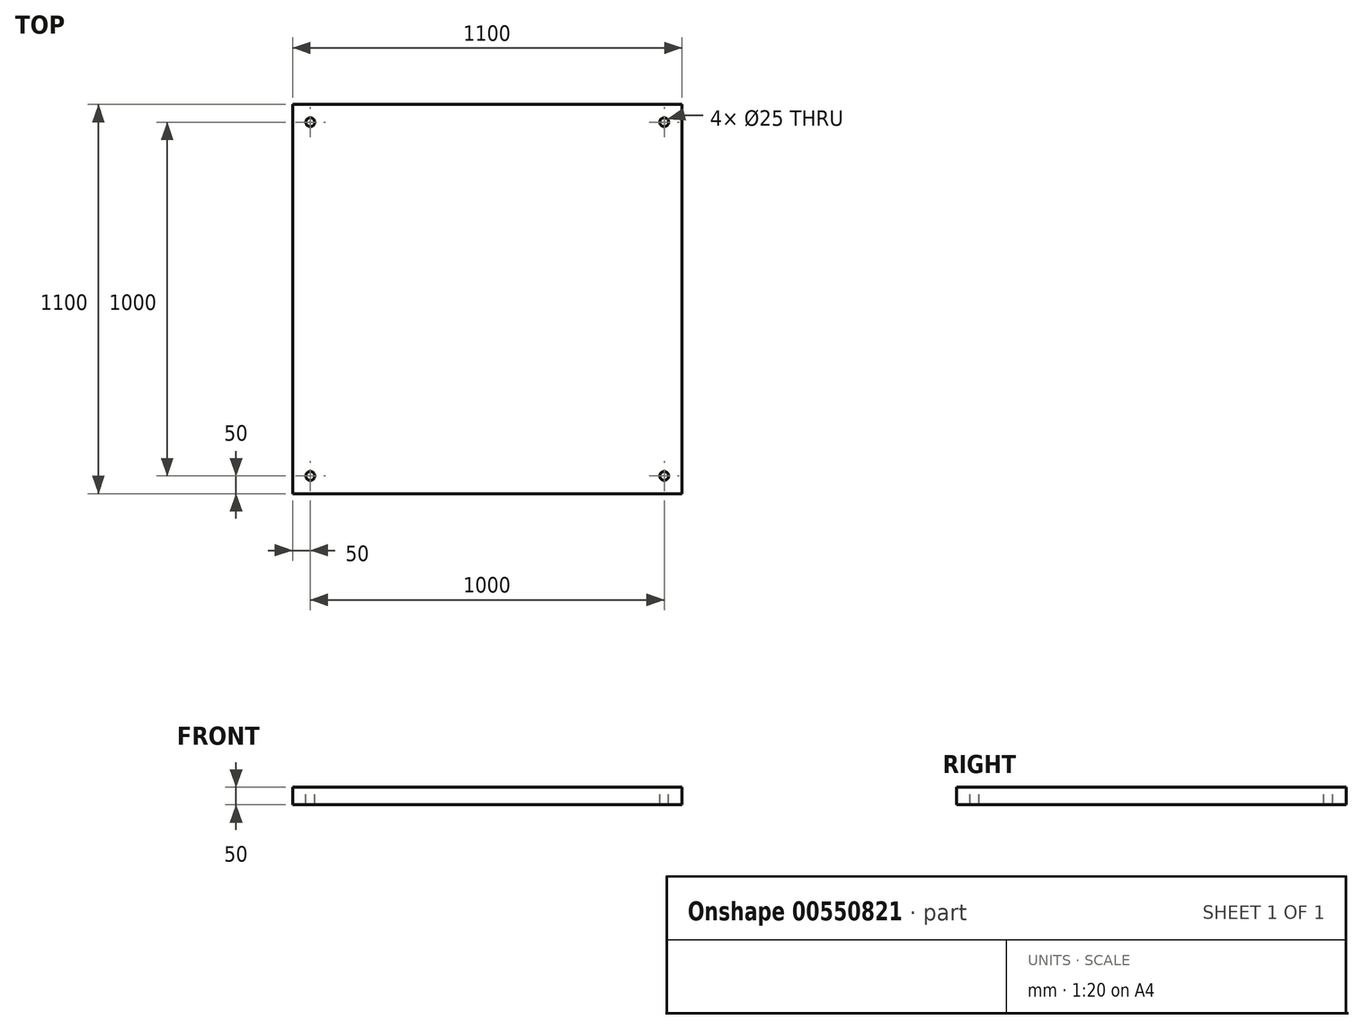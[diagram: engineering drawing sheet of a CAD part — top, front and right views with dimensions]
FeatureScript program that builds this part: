
annotation { "Feature Type Name" : "Feature", "Feature Type Description" : "" }
export const myFeature = defineFeature(function(context is Context, id is Id, definition is map)
    precondition{}
    {
        {
            var Q0;
            Q0=qCreatedBy(makeId("Top.planeOp"),FACE);
            var sketch = newSketch(context, id + "F0", { "sketchPlane" : qUnion([Q0])});
            skLineSegment(sketch, "E0.bottom", {"start": v(550, 550) * mm, "end": v(-550, 550) * mm});
            skLineSegment(sketch, "E0.top", {"start": v(550, -550) * mm, "end": v(-550, -550) * mm});
            skLineSegment(sketch, "E0.left", {"start": v(550, 550) * mm, "end": v(550, -550) * mm});
            skLineSegment(sketch, "E0.right", {"start": v(-550, 550) * mm, "end": v(-550, -550) * mm});
            skPoint(sketch, "E0.middle", {"position": v(0, 0) * mm});
            skSolve(sketch);
        }
        {
            var Q0;
            Q0=makeQuery(id+"F0.imprint","IMPRINT",FACE,{"disambiguationData":[TD([[makeQuery(id+"F0.imprint","IMPRINT",EDGE,{"derivedFrom":sQuery(id+"F0.wireOp",EDGE,"E0.bottom")}),1.0]])]});
            extrude(context, id + "F1", {"entities" : qUnion([Q0]), "depth" : 50 * mm, "offsetDistance" : 25 * mm});
        }
        {
            var Q0;
            Q0=makeQuery(id+"F1.opExtrude","CAP_FACE",FACE,{"disambiguationData":[OSD([sQuery(id+"F0.wireOp",EDGE,"E0.bottom"),sQuery(id+"F0.wireOp",EDGE,"E0.top"),sQuery(id+"F0.wireOp",EDGE,"E0.left"),sQuery(id+"F0.wireOp",EDGE,"E0.right")])],"isStart":false});
            var sketch = newSketch(context, id + "F2", { "sketchPlane" : qUnion([Q0])});
            skCircle(sketch, "E1", {"center": v(500, -500) * mm, "radius": 12.5 * mm});
            skCircle(sketch, "E2", {"center": v(-500, -500) * mm, "radius": 12.5 * mm});
            skCircle(sketch, "E3", {"center": v(-500, 500) * mm, "radius": 12.5 * mm});
            skCircle(sketch, "E4", {"center": v(500, 500) * mm, "radius": 12.5 * mm});
            skSolve(sketch);
        }
        {
            var Q0;
            Q0=makeQuery(id+"F2.imprint","IMPRINT",FACE,{"disambiguationData":[TD([[makeQuery(id+"F2.imprint","IMPRINT",EDGE,{"derivedFrom":sQuery(id+"F2.wireOp",EDGE,"E1")}),1.0]])]});
            var Q1;
            Q1=makeQuery(id+"F2.imprint","IMPRINT",FACE,{"disambiguationData":[TD([[makeQuery(id+"F2.imprint","IMPRINT",EDGE,{"derivedFrom":sQuery(id+"F2.wireOp",EDGE,"E2")}),1.0]])]});
            var Q2;
            Q2=makeQuery(id+"F2.imprint","IMPRINT",FACE,{"disambiguationData":[TD([[makeQuery(id+"F2.imprint","IMPRINT",EDGE,{"derivedFrom":sQuery(id+"F2.wireOp",EDGE,"E3")}),1.0]])]});
            var Q3;
            Q3=makeQuery(id+"F2.imprint","IMPRINT",FACE,{"disambiguationData":[TD([[makeQuery(id+"F2.imprint","IMPRINT",EDGE,{"derivedFrom":sQuery(id+"F2.wireOp",EDGE,"E4")}),1.0]])]});
            extrude(context, id + "F3", {"entities" : qUnion([Q0, Q1, Q2, Q3]), "operationType" : NewBodyOperationType.REMOVE, "oppositeDirection" : true, "depth" : 50 * mm, "offsetDistance" : 25 * mm});
        }
    });
